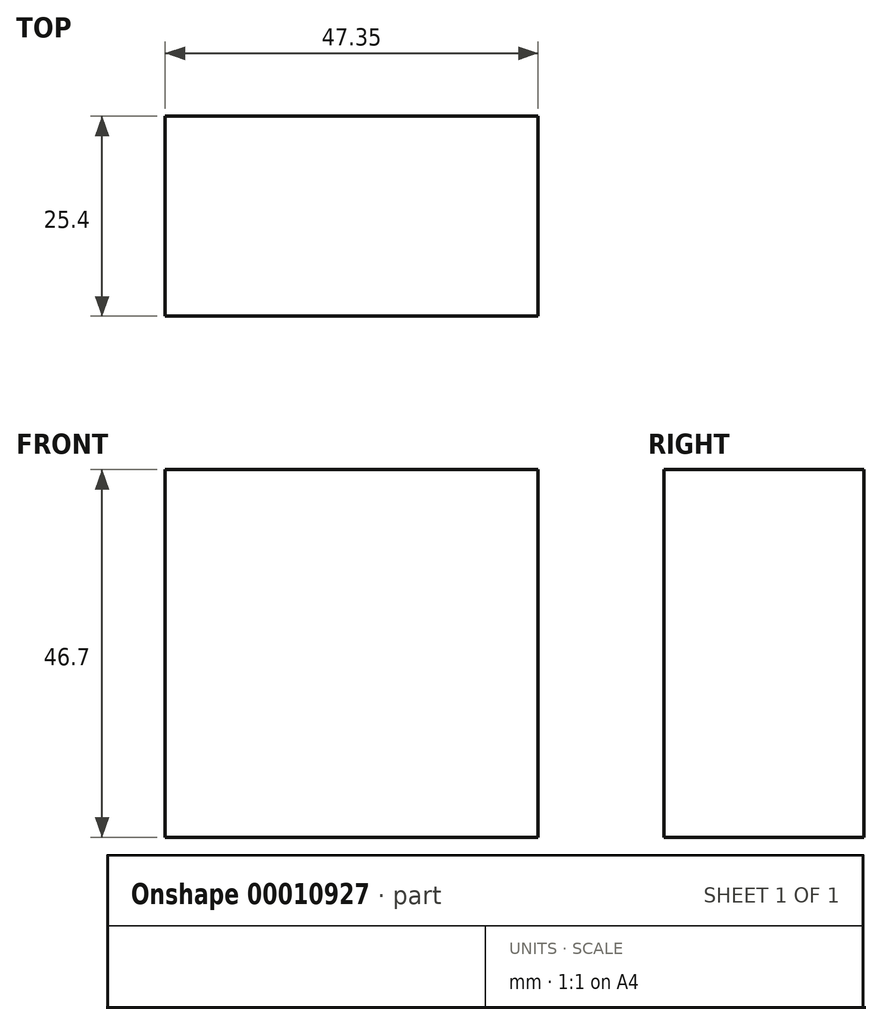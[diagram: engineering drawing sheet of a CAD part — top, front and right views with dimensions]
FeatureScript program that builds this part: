
annotation { "Feature Type Name" : "Feature", "Feature Type Description" : "" }
export const myFeature = defineFeature(function(context is Context, id is Id, definition is map)
    precondition{}
    {
        {
            var Q0;
            Q0=qCreatedBy(makeId("Front.planeOp"),FACE);
            var sketch = newSketch(context, id + "F0", { "sketchPlane" : qUnion([Q0])});
            skLineSegment(sketch, "E0.bottom", {"start": v(0, 0) * mm, "end": v(47.35, 0) * mm});
            skLineSegment(sketch, "E0.top", {"start": v(0, -46.7) * mm, "end": v(47.35, -46.7) * mm});
            skLineSegment(sketch, "E0.left", {"start": v(0, 0) * mm, "end": v(0, -46.7) * mm});
            skLineSegment(sketch, "E0.right", {"start": v(47.35, 0) * mm, "end": v(47.35, -46.7) * mm});
            skSolve(sketch);
        }
        {
            var Q0;
            Q0 = qSketchRegion(id + "F0", true);
            extrude(context, id + "F1", {"entities" : qUnion([Q0]), "depth" : 25.4 * mm});
        }
    });
